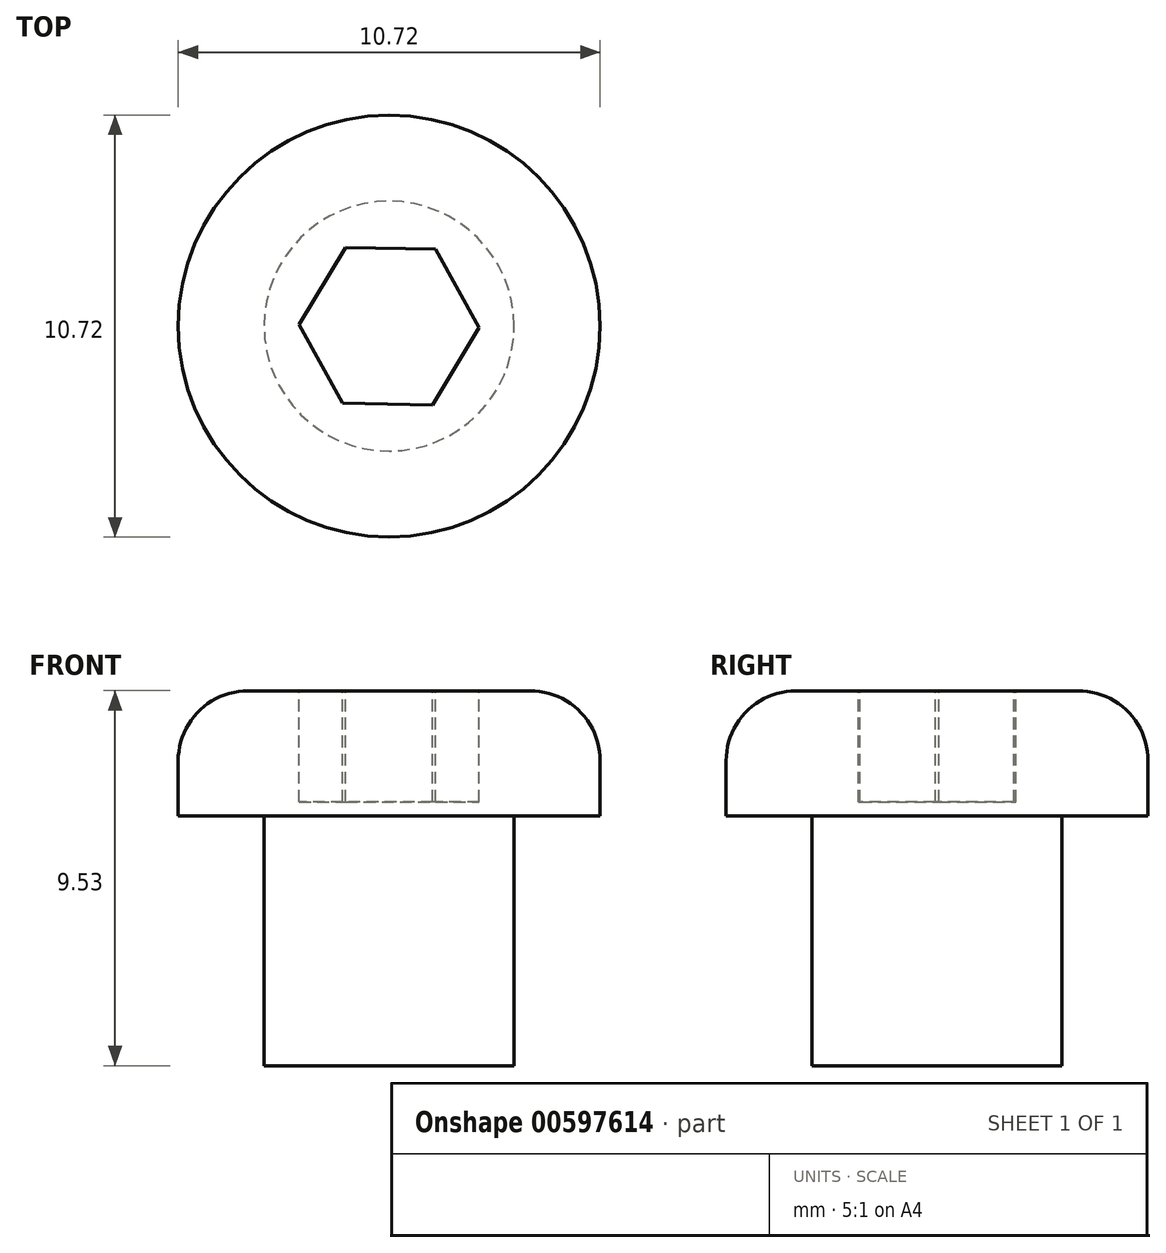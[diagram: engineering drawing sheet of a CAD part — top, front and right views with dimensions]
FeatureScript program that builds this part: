
annotation { "Feature Type Name" : "Feature", "Feature Type Description" : "" }
export const myFeature = defineFeature(function(context is Context, id is Id, definition is map)
    precondition{}
    {
        {
            var Q0;
            Q0=qCreatedBy(makeId("Top.planeOp"),FACE);
            var sketch = newSketch(context, id + "F0", { "sketchPlane" : qUnion([Q0])});
            skCircle(sketch, "E0", {"center": v(0, 0) * mm, "radius": 3.18 * mm});
            skSolve(sketch);
        }
        {
            var Q0;
            Q0=qSketchRegion(id+"F0",true);
            extrude(context, id + "F1", {"entities" : qUnion([Q0]), "depth" : 6.35 * mm});
        }
        {
            var Q0;
            Q0=makeQuery(id+"F1.opExtrude","CAP_FACE",FACE,{"disambiguationData":[OSD([sQuery(id+"F0.wireOp",EDGE,"E0")])],"isStart":false});
            var sketch = newSketch(context, id + "F2", { "sketchPlane" : qUnion([Q0])});
            skCircle(sketch, "E1", {"center": v(0, 0) * mm, "radius": 5.36 * mm});
            skSolve(sketch);
        }
        {
            var Q0;
            Q0=qSketchRegion(id+"F2",true);
            extrude(context, id + "F3", {"entities" : qUnion([Q0]), "operationType" : NewBodyOperationType.ADD, "depth" : 0.79 * mm});
        }
        {
            var Q0;
            Q0=makeQuery(id+"F3.opExtrude","CAP_FACE",FACE,{"disambiguationData":[OSD([sQuery(id+"F2.wireOp",EDGE,"E1")])],"isStart":false});
            var sketch = newSketch(context, id + "F4", { "sketchPlane" : qUnion([Q0])});
            skCircle(sketch, "E2", {"center": v(0, 0) * mm, "radius": 5.36 * mm});
            skSolve(sketch);
        }
        {
            var Q0;
            Q0=qSketchRegion(id+"F4",true);
            extrude(context, id + "F5", {"entities" : qUnion([Q0]), "operationType" : NewBodyOperationType.ADD, "depth" : 2.4 * mm});
        }
        {
            var Q0;
            Q0=makeQuery(id+"F5.opExtrude","CAP_EDGE",EDGE,{"disambiguationData":[OSD([sQuery(id+"F4.wireOp",EDGE,"E2")])],"isStart":false});
            fillet(context, id + "F6", {"entities" : qUnion([Q0]), "radius" : 1.78 * mm, "tangentPropagation" : true, "allowEdgeOverflow" : false});
        }
        {
            var Q0;
            Q0=makeQuery(id+"F5.opExtrude","CAP_FACE",FACE,{"disambiguationData":[OSD([sQuery(id+"F4.wireOp",EDGE,"E2")])],"isStart":false});
            var sketch = newSketch(context, id + "F7", { "sketchPlane" : qUnion([Q0])});
            skCircle(sketch, "E3.cCircle", {"center": v(0, 0) * mm, "radius": 1.98 * mm, "construction": true});
            skLineSegment(sketch, "E3.0", {"start": v(2.29, -0.04) * mm, "end": v(1.1, -2) * mm});
            skLineSegment(sketch, "E3.1", {"start": v(1.1, -2) * mm, "end": v(-1.18, -1.96) * mm});
            skLineSegment(sketch, "E3.2", {"start": v(-1.18, -1.96) * mm, "end": v(-2.29, 0.04) * mm});
            skLineSegment(sketch, "E3.3", {"start": v(-2.29, 0.04) * mm, "end": v(-1.1, 2) * mm});
            skLineSegment(sketch, "E3.4", {"start": v(-1.1, 2) * mm, "end": v(1.18, 1.96) * mm});
            skLineSegment(sketch, "E3.5", {"start": v(1.18, 1.96) * mm, "end": v(2.29, -0.04) * mm});
            skPoint(sketch, "E3.0.midPoint", {"position": v(1.7, -1.02) * mm});
            skSolve(sketch);
        }
        {
            var Q0;
            Q0=qSketchRegion(id+"F7",true);
            extrude(context, id + "F8", {"entities" : qUnion([Q0]), "operationType" : NewBodyOperationType.REMOVE, "oppositeDirection" : true, "depth" : 2.82 * mm});
        }
    });
